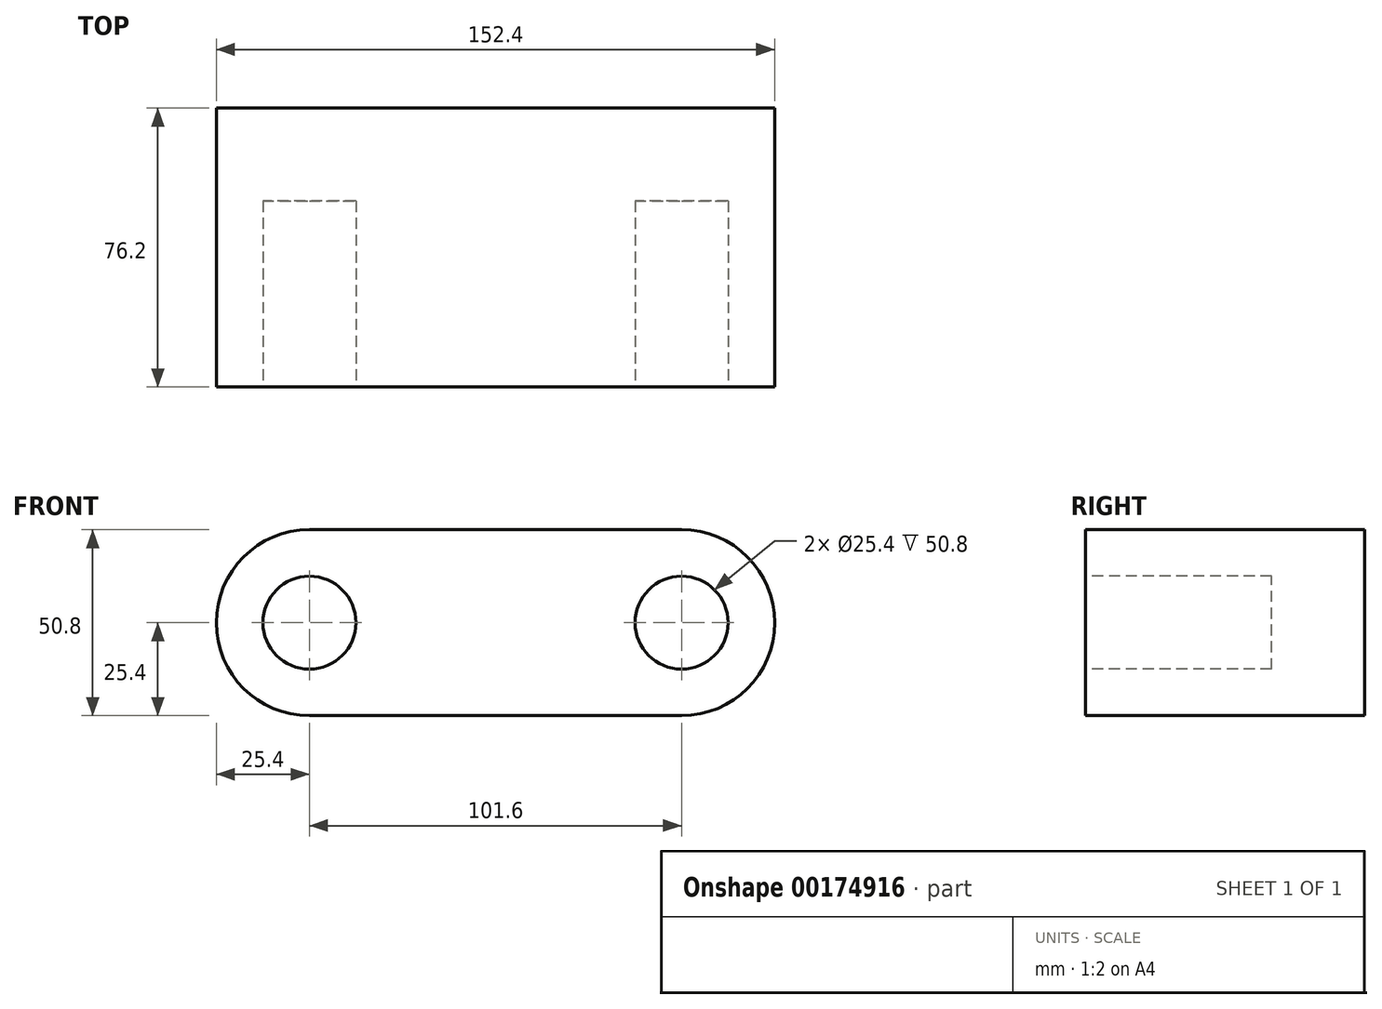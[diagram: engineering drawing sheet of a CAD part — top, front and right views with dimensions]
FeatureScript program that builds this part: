
annotation { "Feature Type Name" : "Feature", "Feature Type Description" : "" }
export const myFeature = defineFeature(function(context is Context, id is Id, definition is map)
    precondition{}
    {
        {
            var Q0;
            Q0=qCreatedBy(makeId("Front.planeOp"),FACE);
            var sketch = newSketch(context, id + "F0", { "sketchPlane" : qUnion([Q0])});
            skLineSegment(sketch, "E0.bottom", {"start": v(0, 0) * mm, "end": v(-101.6, 0) * mm});
            skLineSegment(sketch, "E0.top", {"start": v(0, 50.8) * mm, "end": v(-101.6, 50.8) * mm});
            skLineSegment(sketch, "E0.left", {"start": v(0, 0) * mm, "end": v(0, 50.8) * mm});
            skLineSegment(sketch, "E0.right", {"start": v(-101.6, 0) * mm, "end": v(-101.6, 50.8) * mm});
            skArc(sketch, "E1", {"start": v(-101.6, 50.8) * mm, "mid": v(-127, 25.4) * mm, "end": v(-101.6, 0) * mm});
            skArc(sketch, "E2", {"start": v(0, 0) * mm, "mid": v(25.4, 25.4) * mm, "end": v(0, 50.8) * mm});
            skSolve(sketch);
        }
        {
            var Q0;
            Q0=makeQuery(id+"F0.imprint","IMPRINT",FACE,{"disambiguationData":[TD([[makeQuery(id+"F0.imprint","IMPRINT",EDGE,{"derivedFrom":sQuery(id+"F0.wireOp",EDGE,"E0.right")}),1.0]])]});
            var Q1;
            Q1=makeQuery(id+"F0.imprint","IMPRINT",FACE,{"disambiguationData":[TD([[makeQuery(id+"F0.imprint","IMPRINT",EDGE,{"derivedFrom":sQuery(id+"F0.wireOp",EDGE,"E0.bottom")}),-1.0]])]});
            var Q2;
            Q2=makeQuery(id+"F0.imprint","IMPRINT",FACE,{"disambiguationData":[TD([[makeQuery(id+"F0.imprint","IMPRINT",EDGE,{"derivedFrom":sQuery(id+"F0.wireOp",EDGE,"E0.left")}),-1.0]])]});
            extrude(context, id + "F1", {"entities" : qUnion([Q0, Q1, Q2]), "depth" : 76.2 * mm});
        }
        {
            var Q0;
            Q0=makeQuery(id+"F1.opExtrude","CAP_FACE",FACE,{"disambiguationData":[OSD([sQuery(id+"F0.wireOp",EDGE,"E0.bottom"),sQuery(id+"F0.wireOp",EDGE,"E0.top"),sQuery(id+"F0.wireOp",EDGE,"E1"),sQuery(id+"F0.wireOp",EDGE,"E2")])],"isStart":false});
            var sketch = newSketch(context, id + "F2", { "sketchPlane" : qUnion([Q0])});
            skCircle(sketch, "E3", {"center": v(-101.6, 25.4) * mm, "radius": 12.7 * mm});
            skCircle(sketch, "E4", {"center": v(0, 25.4) * mm, "radius": 12.7 * mm});
            skSolve(sketch);
        }
        {
            var Q0;
            Q0=makeQuery(id+"F2.imprint","IMPRINT",FACE,{"disambiguationData":[TD([[makeQuery(id+"F2.imprint","IMPRINT",EDGE,{"derivedFrom":sQuery(id+"F2.wireOp",EDGE,"E4")}),1.0]])]});
            var Q1;
            Q1=makeQuery(id+"F2.imprint","IMPRINT",FACE,{"disambiguationData":[TD([[makeQuery(id+"F2.imprint","IMPRINT",EDGE,{"derivedFrom":sQuery(id+"F2.wireOp",EDGE,"E3")}),1.0]])]});
            extrude(context, id + "F3", {"entities" : qUnion([Q0, Q1]), "operationType" : NewBodyOperationType.REMOVE, "oppositeDirection" : true, "depth" : 50.8 * mm});
        }
    });
